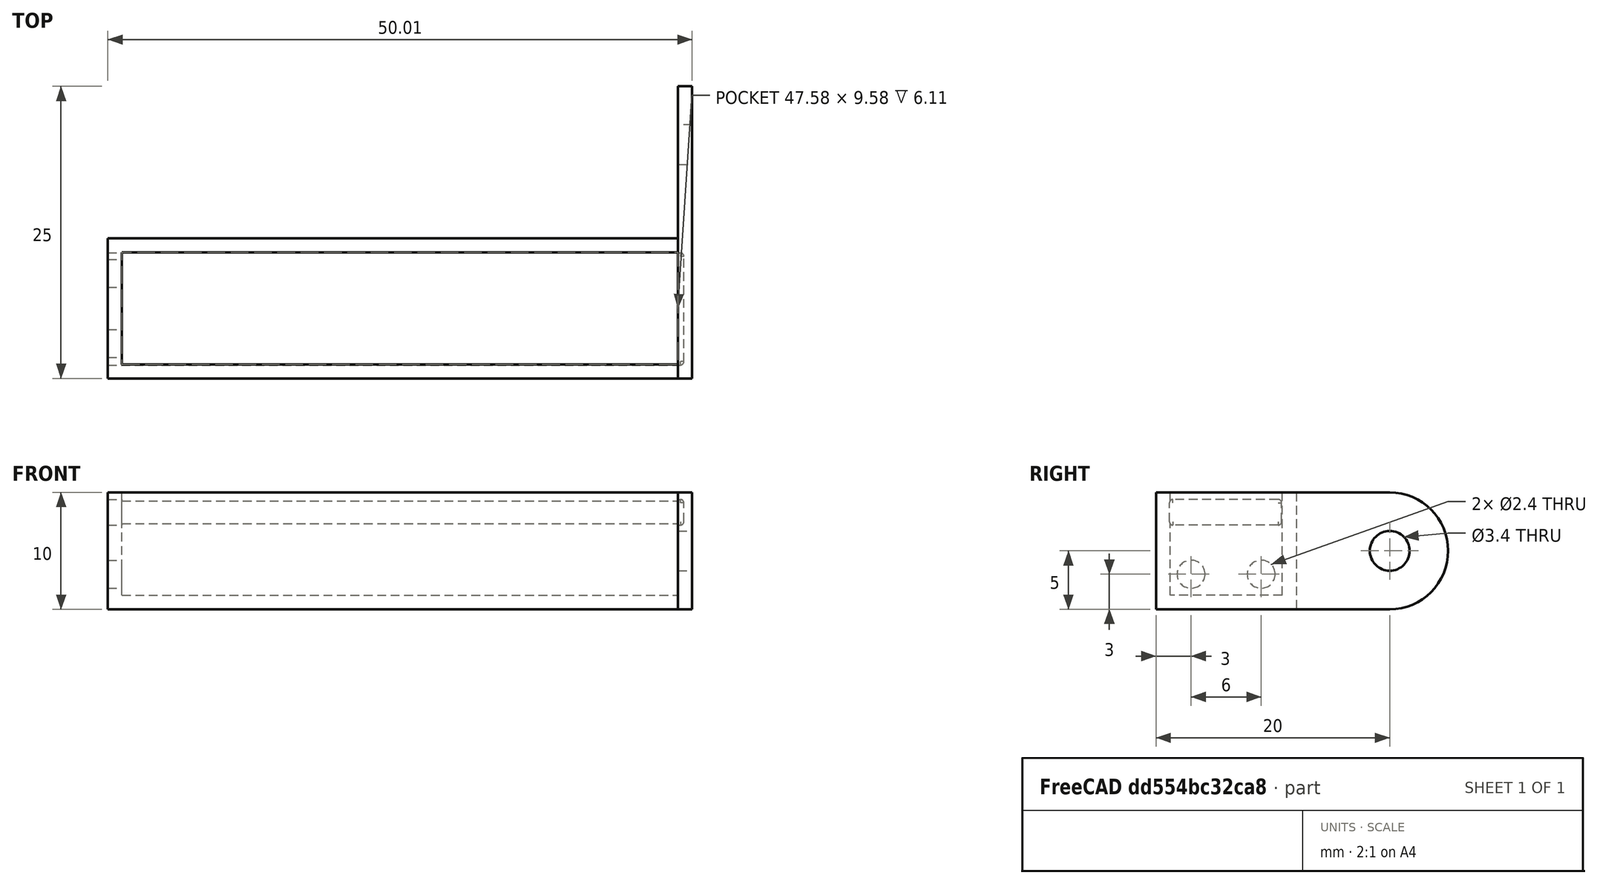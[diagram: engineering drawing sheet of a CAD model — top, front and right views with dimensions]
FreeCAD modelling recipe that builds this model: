
FCSTD DOCUMENT  (FreeCAD 0.14R3702 (Git))
Label: luz
License: CC-BY 3.0
LicenseURL: http://creativecommons.org/licenses/by/3.0/
objects: Part::Box×3, Part::Cylinder×3, Part::Cut×3, Part::MultiFuse×2, Part::Thickness×1, Sketcher::SketchObject×1, PartDesign::Pocket×1, Part::Offset×1
note: 16 computed .brp shape members not serialized (recipe doc carries the construction recipe); baked Part::Feature solids carry a one-line shape summary decoded from their .brp

FEATURE [Part::Box] Box  label="Cube"
  Height = 10
  Length = 50
  Width = 12
FEATURE [Part::Thickness] Thickness  label="Holder"
  Faces = -> Box [Face6]
  Intersection = false
  Join = 0
  Mode = 0
  SelfIntersection = false
  Value = -1.21
FEATURE [Part::Cylinder] Cylinder  label="RedWire"
  Angle = 360
  Height = 10
  Placement = pos=(-3,3,3) rot=(0,1,0;1.5708rad)
  Radius = 1.2
FEATURE [Part::Cylinder] Cylinder001  label="BlackWire"
  Angle = 360
  Height = 10
  Placement = pos=(-3,9,3) rot=(0,1,0;1.5708rad)
  Radius = 1.2
FEATURE [Part::Box] Box001  label="Arm"
  Height = 10
  Length = 1.21
  Placement = pos=(48.8,0,0) rot=(0,0,1;0rad)
  Width = 20
FEATURE [Part::Box] Box002  label="Screen"
  Height = 1.6
  Length = 50
  Placement = pos=(-1,1.45,7.5) rot=(0,0,1;0rad)
  Width = 9
FEATURE [Part::Cylinder] Cylinder002  label="ArmEnding"
  Angle = 180
  Height = 1.21
  Placement = pos=(48.8,20,5) rot=(0,1,0;1.5708rad)
  Radius = 5
FEATURE [Part::MultiFuse] Fusion
  Shapes = -> [Cylinder002,Box001]
FEATURE [Sketcher::SketchObject] Sketch
  ExternalGeometry = -> [Fusion]
  Placement = pos=(50.01,0,0) rot=(0.57735,0.57735,0.57735;2.0944rad)
  Support = -> Fusion [Face3]
  sketch-geometry (2):
    g0: Circle CenterX=20 CenterY=5 CenterZ=0 NormalX=0 NormalY=0 NormalZ=1 Radius=1.7
    g1: GeomPoint [constr] X=20 Y=5 Z=0
  constraints (3):
    c: Coincident(g0,g-3)
    c: Radius(g0) = 1.7
    c: Coincident(g1,g-3)
FEATURE [PartDesign::Pocket] Pocket
  Length = 5
  Sketch = -> Sketch
  Type = 0
FEATURE [Part::Cut] Cut
  Base = -> Thickness
  Tool = -> Cylinder
FEATURE [Part::Cut] Cut001  label="HolderWired"
  Base = -> Cut
  Tool = -> Cylinder001
FEATURE [Part::MultiFuse] Fusion001  label="LightBarWithoutScreen"
  Shapes = -> [Cut001,Pocket]
FEATURE [Part::Offset] Offset  label="ScreenPocket"
  Fill = false
  Intersection = false
  Join = 0
  Mode = 0
  SelfIntersection = false
  Source = -> Box002
  Value = 0.3
FEATURE [Part::Cut] Cut002  label="LightBar"
  Base = -> Fusion001
  Tool = -> Offset
